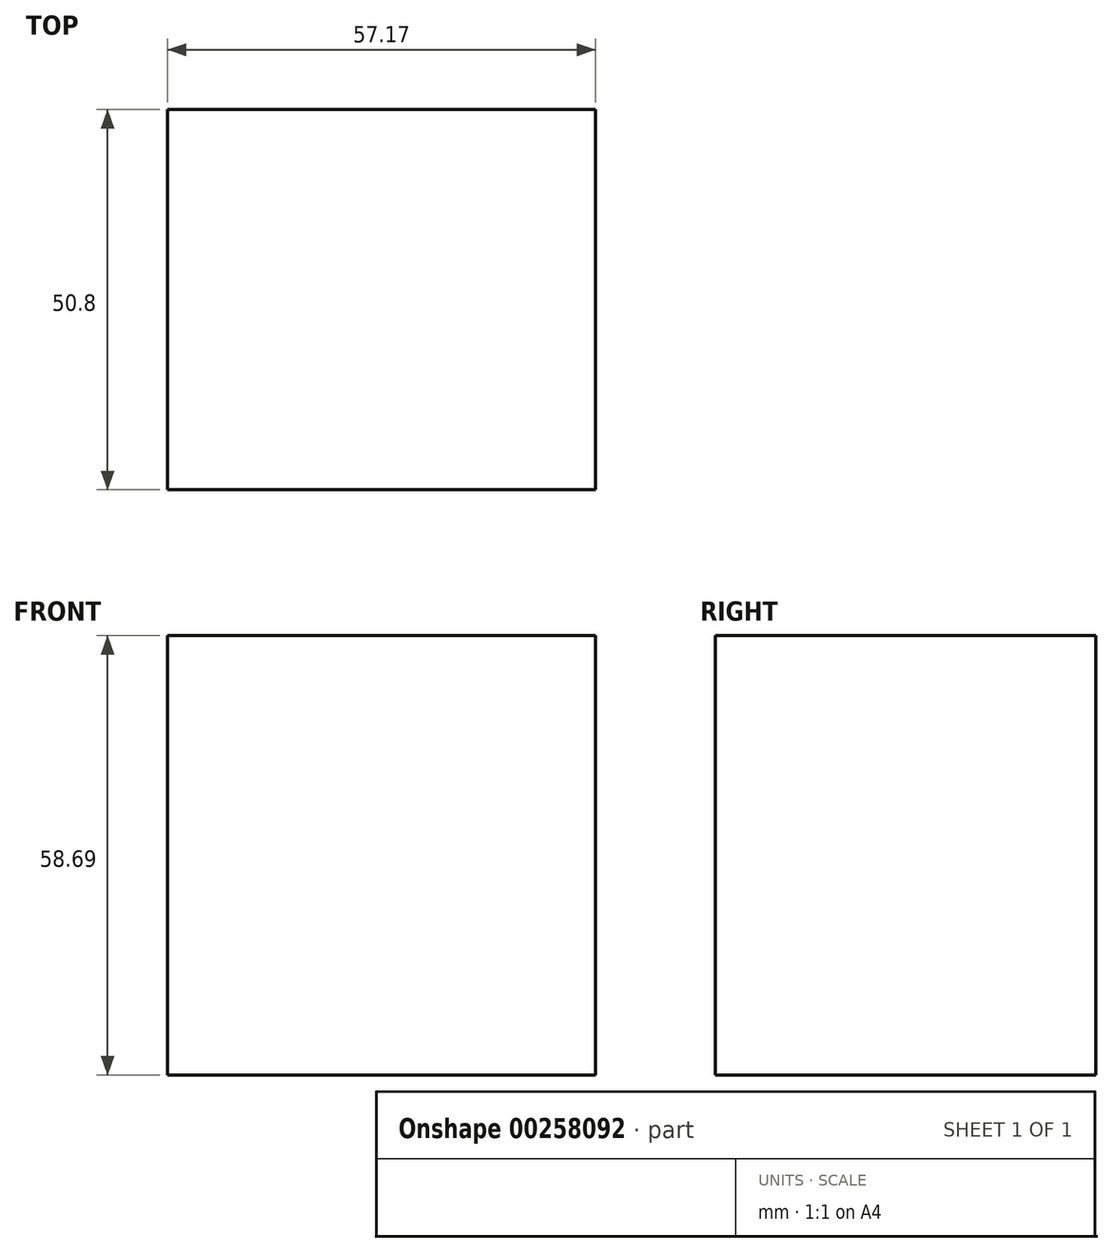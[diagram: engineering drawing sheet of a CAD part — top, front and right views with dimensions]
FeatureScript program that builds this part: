
annotation { "Feature Type Name" : "Feature", "Feature Type Description" : "" }
export const myFeature = defineFeature(function(context is Context, id is Id, definition is map)
    precondition{}
    {
        {
            var Q0;
            Q0=qCreatedBy(makeId("Front.planeOp"),FACE);
            var sketch = newSketch(context, id + "F0", { "sketchPlane" : qUnion([Q0])});
            skLineSegment(sketch, "E0.bottom", {"start": v(0, 0) * mm, "end": v(-57.17, 0) * mm});
            skLineSegment(sketch, "E0.top", {"start": v(0, 58.69) * mm, "end": v(-57.17, 58.69) * mm});
            skLineSegment(sketch, "E0.left", {"start": v(0, 0) * mm, "end": v(0, 58.69) * mm});
            skLineSegment(sketch, "E0.right", {"start": v(-57.17, 0) * mm, "end": v(-57.17, 58.69) * mm});
            skSolve(sketch);
        }
        {
            var Q0;
            Q0=makeQuery(id+"F0.imprint","IMPRINT",FACE,{"disambiguationData":[TD([[makeQuery(id+"F0.imprint","IMPRINT",EDGE,{"derivedFrom":sQuery(id+"F0.wireOp",EDGE,"E0.bottom")}),-1.0]])]});
            extrude(context, id + "F1", {"entities" : qUnion([Q0]), "depth" : 50.8 * mm});
        }
    });
